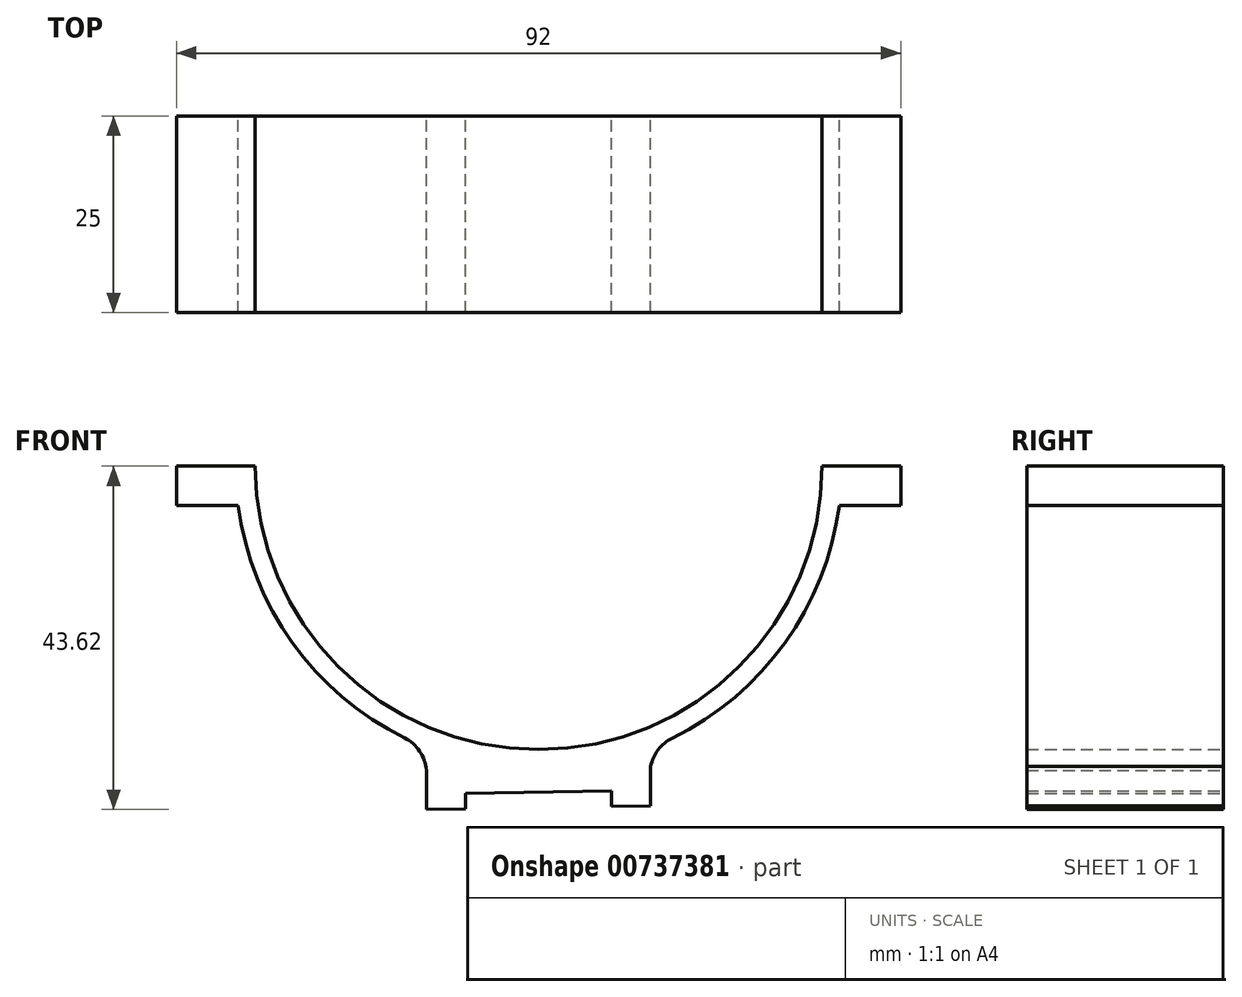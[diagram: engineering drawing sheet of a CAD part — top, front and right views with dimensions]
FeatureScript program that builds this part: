
annotation { "Feature Type Name" : "Feature", "Feature Type Description" : "" }
export const myFeature = defineFeature(function(context is Context, id is Id, definition is map)
    precondition{}
    {
        {
            var Q0;
            Q0=qCreatedBy(makeId("Front.planeOp"),FACE);
            var sketch = newSketch(context, id + "F0", { "sketchPlane" : qUnion([Q0])});
            skArc(sketch, "E0", {"start": v(-36, 0) * mm, "mid": v(0, -36) * mm, "end": v(36, 0) * mm});
            skArc(sketch, "E1", {"start": v(-38.17, -5) * mm, "mid": v(-26.3, -28.12) * mm, "end": v(-2.44, -38.42) * mm});
            skLineSegment(sketch, "E2", {"start": v(-38.5, 0) * mm, "end": v(-36, 0) * mm});
            skLineSegment(sketch, "E3.bottom", {"start": v(36, 0) * mm, "end": v(46, 0) * mm});
            skLineSegment(sketch, "E3.top", {"start": v(38.17, -5) * mm, "end": v(46, -5) * mm});
            skLineSegment(sketch, "E3.right", {"start": v(46, 0) * mm, "end": v(46, -5) * mm});
            skLineSegment(sketch, "E4.bottom", {"start": v(-36, 0) * mm, "end": v(-46, 0) * mm});
            skLineSegment(sketch, "E4.top", {"start": v(-38.17, -5) * mm, "end": v(-46, -5) * mm});
            skLineSegment(sketch, "E4.left", {"start": v(-36, 0) * mm, "end": v(-36, -5) * mm});
            skLineSegment(sketch, "E4.right", {"start": v(-46, 0) * mm, "end": v(-46, -5) * mm});
            skLineSegment(sketch, "E5.bottom", {"start": v(14.22, -38.15) * mm, "end": v(3.7, -38.32) * mm});
            skPoint(sketch, "E5.middle", {"position": v(-0.03, -43.38) * mm});
            skPoint(sketch, "E5.middle.positionSnap0", {"position": v(-0.03, -38.5) * mm});
            skPoint(sketch, "E5.centerSnap0", {"position": v(-0.03, -38.5) * mm});
            skLineSegment(sketch, "E6", {"start": v(9.22, -43.23) * mm, "end": v(14.22, -43.15) * mm});
            skLineSegment(sketch, "E7.trimOffspring", {"start": v(-2.44, -38.42) * mm, "end": v(-14.28, -38.62) * mm});
            skArc(sketch, "E8.trimOffspring", {"start": v(3.7, -38.32) * mm, "mid": v(26.76, -27.68) * mm, "end": v(38.17, -5) * mm});
            skPoint(sketch, "E5.top.start.orphan", {"position": v(16.83, -48.1) * mm});
            skPoint(sketch, "E9.orphan", {"position": v(-16.88, -48.66) * mm});
            skLineSegment(sketch, "E10.trimOffspring", {"start": v(36, 0) * mm, "end": v(38.5, 0) * mm});
            skPoint(sketch, "E11.startSnap0", {"position": v(-9.66, -38.54) * mm});
            skLineSegment(sketch, "E12.bottom", {"start": v(-9.28, -41.54) * mm, "end": v(9.22, -41.23) * mm});
            skLineSegment(sketch, "E12.left", {"start": v(-9.28, -41.54) * mm, "end": v(-9.28, -43.54) * mm});
            skLineSegment(sketch, "E12.right", {"start": v(9.22, -41.23) * mm, "end": v(9.22, -43.23) * mm});
            skLineSegment(sketch, "E13.trimOffspring", {"start": v(-9.28, -43.54) * mm, "end": v(-14.28, -43.62) * mm});
            skPoint(sketch, "E14.orphan", {"position": v(-9.28, -45.54) * mm});
            skPoint(sketch, "E15.orphan", {"position": v(9.22, -45.23) * mm});
            skLineSegment(sketch, "E16", {"start": v(-14.28, -43.62) * mm, "end": v(-14.28, -38.62) * mm});
            skLineSegment(sketch, "E17", {"start": v(14.22, -43.15) * mm, "end": v(14.22, -38.15) * mm});
            skPoint(sketch, "E5.right.end.orphan", {"position": v(-16.88, -43.66) * mm});
            skPoint(sketch, "E18.orphan", {"position": v(-16.89, -38.66) * mm});
            skPoint(sketch, "E19.orphan", {"position": v(16.83, -38.1) * mm});
            skPoint(sketch, "E20.orphan", {"position": v(16.83, -43.1) * mm});
            skSolve(sketch);
        }
        {
            var Q0;
            {var subQ2=sQuery(id+"F0.wireOp",EDGE,"E0");Q0=makeQuery(id+"F0.imprint","IMPRINT",FACE,{"disambiguationData":[TD([[makeQuery(id+"F0.imprint","IMPRINT",EDGE,{"derivedFrom":subQ2}),-1.0]])]});}
            extrude(context, id + "F1", {"entities" : qUnion([Q0]), "depth" : 25 * mm, "offsetDistance" : 25 * mm});
        }
        {
            var Q0;
            Q0=makeQuery(id+"F1.opExtrude","SWEPT_EDGE",EDGE,{"disambiguationData":[OSD([sQuery(id+"F0.wireOp",EDGE,"E1"),sQuery(id+"F0.wireOp",EDGE,"E7.trimOffspring")])]});
            var Q1;
            Q1=makeQuery(id+"F1.opExtrude","SWEPT_EDGE",EDGE,{"disambiguationData":[OSD([sQuery(id+"F0.wireOp",EDGE,"E5.bottom"),sQuery(id+"F0.wireOp",EDGE,"E8.trimOffspring")])]});
            fillet(context, id + "F2", {"entities" : qUnion([Q0, Q1]), "radius" : 5 * mm, "tangentPropagation" : true, "allowEdgeOverflow" : false});
        }
    });
